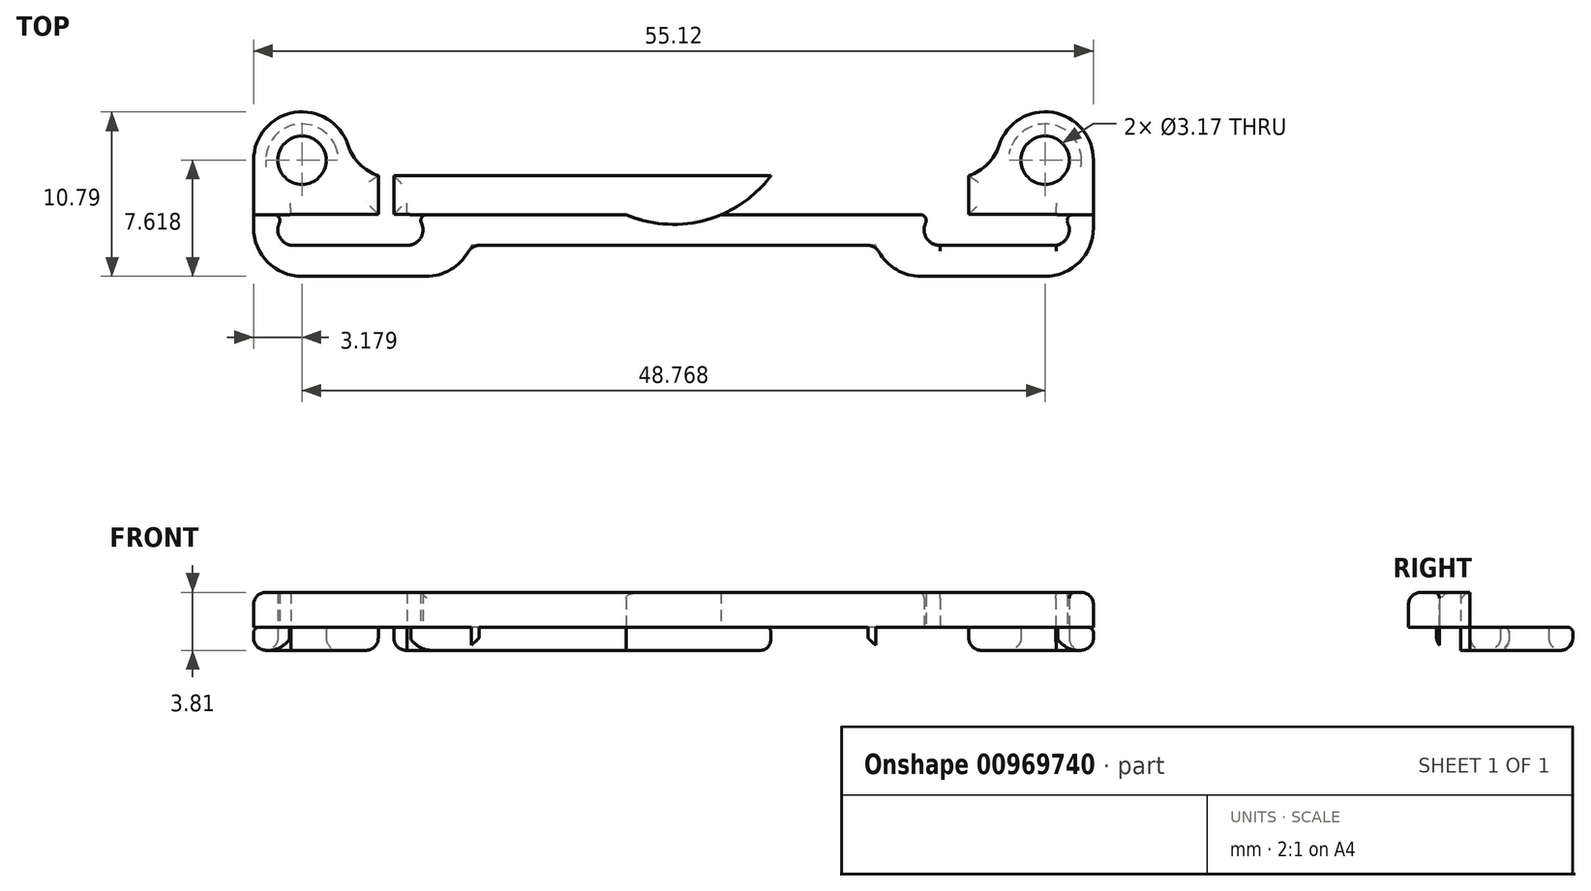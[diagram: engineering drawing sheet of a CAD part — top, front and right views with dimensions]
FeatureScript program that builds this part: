
annotation { "Feature Type Name" : "Feature", "Feature Type Description" : "" }
export const myFeature = defineFeature(function(context is Context, id is Id, definition is map)
    precondition{}
    {
        {
            var Q0;
            Q0=qCreatedBy(makeId("Top.planeOp"),FACE);
            var sketch = newSketch(context, id + "F0", { "sketchPlane" : qUnion([Q0])});
            skLineSegment(sketch, "E0", {"start": v(-29.34, -33.33) * mm, "end": v(-29.34, -17.07) * mm});
            skLineSegment(sketch, "E1", {"start": v(-32.75, -29.77) * mm, "end": v(29.96, -29.77) * mm, "construction": true});
            skLineSegment(sketch, "E2", {"start": v(-25.78, 34.73) * mm, "end": v(-25.78, -35.44) * mm, "construction": true});
            skLineSegment(sketch, "E3", {"start": v(22.99, 35.22) * mm, "end": v(22.99, -36.91) * mm, "construction": true});
            skCircle(sketch, "E4", {"center": v(-25.78, -29.77) * mm, "radius": 1.59 * mm});
            skCircle(sketch, "E5", {"center": v(22.99, -29.77) * mm, "radius": 1.59 * mm});
            skArc(sketch, "E6", {"start": v(-22.77, -30.79) * mm, "mid": v(-25.27, -26.64) * mm, "end": v(-28.96, -29.77) * mm});
            skArc(sketch, "E7", {"start": v(22.99, -32.95) * mm, "mid": v(24.84, -27.2) * mm, "end": v(19.98, -30.79) * mm});
            skLineSegment(sketch, "E8", {"start": v(-29.34, -33.33) * mm, "end": v(-29.34, -44.2) * mm});
            skLineSegment(sketch, "E9", {"start": v(-28.96, -37.4) * mm, "end": v(-14.67, -37.4) * mm});
            skLineSegment(sketch, "E10", {"start": v(-14.67, -35.36) * mm, "end": v(-14.67, -37.4) * mm});
            skLineSegment(sketch, "E11", {"start": v(-28.96, -29.77) * mm, "end": v(-28.96, -37.4) * mm});
            skLineSegment(sketch, "E12.trimOffspring", {"start": v(-18.84, -33.33) * mm, "end": v(-19.76, -33.33) * mm});
            skLineSegment(sketch, "E13.trimOffspring", {"start": v(-14.67, -35.36) * mm, "end": v(-1.4, -35.36) * mm});
            skPoint(sketch, "E14.orphan", {"position": v(-29.34, -37.4) * mm});
            skArc(sketch, "E15", {"start": v(-18.9, -35.36) * mm, "mid": v(-17.84, -34.35) * mm, "end": v(-18.88, -33.33) * mm});
            skArc(sketch, "E16", {"start": v(-26.5, -33.33) * mm, "mid": v(-27.37, -34.34) * mm, "end": v(-26.5, -35.36) * mm});
            skLineSegment(sketch, "E17", {"start": v(-19.76, -33.33) * mm, "end": v(-19.76, -30.79) * mm});
            skLineSegment(sketch, "E18", {"start": v(-20.77, -33.33) * mm, "end": v(-20.77, -30.79) * mm});
            skLineSegment(sketch, "E19.trimOffspring", {"start": v(-26.5, -35.36) * mm, "end": v(-18.82, -35.36) * mm});
            skLineSegment(sketch, "E20.trimOffspring", {"start": v(-27.37, -34.31) * mm, "end": v(-27.37, -34.37) * mm});
            skLineSegment(sketch, "E21.trimOffspring", {"start": v(-20.77, -33.33) * mm, "end": v(-26.5, -33.33) * mm});
            skLineSegment(sketch, "E22.trimOffspring", {"start": v(-19.76, -30.79) * mm, "end": v(-1.4, -30.79) * mm});
            skLineSegment(sketch, "E23.trimOffspring", {"start": v(-22.77, -30.79) * mm, "end": v(-20.77, -30.79) * mm});
            skLineSegment(sketch, "E24", {"start": v(-1.4, -30.79) * mm, "end": v(-1.4, -40.59) * mm});
            skLineSegment(sketch, "E25.MirrorCS", {"start": v(19.98, -30.79) * mm, "end": v(17.98, -30.79) * mm});
            skLineSegment(sketch, "E26.MirrorCS", {"start": v(17.98, -33.33) * mm, "end": v(17.98, -30.79) * mm});
            skLineSegment(sketch, "E27.MirrorCS", {"start": v(16.96, -33.33) * mm, "end": v(16.96, -30.79) * mm});
            skLineSegment(sketch, "E28.MirrorCS", {"start": v(16.96, -30.79) * mm, "end": v(-1.4, -30.79) * mm});
            skLineSegment(sketch, "E29.MirrorCS", {"start": v(16.04, -33.33) * mm, "end": v(16.96, -33.33) * mm});
            skArc(sketch, "E30.MirrorCS", {"start": v(16.1, -35.36) * mm, "mid": v(15.05, -34.35) * mm, "end": v(16.09, -33.33) * mm});
            skLineSegment(sketch, "E31.MirrorCS", {"start": v(23.7, -35.36) * mm, "end": v(16.03, -35.36) * mm});
            skArc(sketch, "E32.MirrorCS", {"start": v(23.7, -33.33) * mm, "mid": v(24.57, -34.34) * mm, "end": v(23.7, -35.36) * mm});
            skLineSegment(sketch, "E33.MirrorCS", {"start": v(17.98, -33.33) * mm, "end": v(23.7, -33.33) * mm});
            skLineSegment(sketch, "E34.MirrorCS", {"start": v(26.16, -29.77) * mm, "end": v(26.16, -37.4) * mm});
            skLineSegment(sketch, "E35.MirrorCS", {"start": v(26.16, -37.4) * mm, "end": v(11.87, -37.4) * mm});
            skLineSegment(sketch, "E36.MirrorCS", {"start": v(11.87, -35.36) * mm, "end": v(11.87, -37.4) * mm});
            skLineSegment(sketch, "E37.MirrorCS", {"start": v(11.87, -35.36) * mm, "end": v(-1.4, -35.36) * mm});
            skSolve(sketch);
        }
        {
            var Q0;
            Q0=makeQuery(id+"F0.imprint","IMPRINT",FACE,{"disambiguationData":[TD([[makeQuery(id+"F0.imprint","IMPRINT",EDGE,{"derivedFrom":sQuery(id+"F0.wireOp",EDGE,"E5")}),-1.0]])]});
            var Q1;
            Q1=makeQuery(id+"F0.imprint","IMPRINT",FACE,{"disambiguationData":[TD([[makeQuery(id+"F0.imprint","IMPRINT",EDGE,{"derivedFrom":sQuery(id+"F0.wireOp",EDGE,"E4")}),-1.0]])]});
            extrude(context, id + "F1", {"entities" : qUnion([Q0, Q1]), "depth" : 1.52 * mm, "offsetDistance" : 25.4 * mm});
        }
        {
            var Q0;
            Q0=makeQuery(id+"F1.opExtrude","CAP_FACE",FACE,{"disambiguationData":[OSD([sQuery(id+"F0.wireOp",EDGE,"E4"),sQuery(id+"F0.wireOp",EDGE,"E5"),sQuery(id+"F0.wireOp",EDGE,"E6"),sQuery(id+"F0.wireOp",EDGE,"E7"),sQuery(id+"F0.wireOp",EDGE,"E9"),sQuery(id+"F0.wireOp",EDGE,"E10"),sQuery(id+"F0.wireOp",EDGE,"E11"),sQuery(id+"F0.wireOp",EDGE,"E12.trimOffspring"),sQuery(id+"F0.wireOp",EDGE,"E13.trimOffspring"),sQuery(id+"F0.wireOp",EDGE,"E15"),sQuery(id+"F0.wireOp",EDGE,"E16"),sQuery(id+"F0.wireOp",EDGE,"E17"),sQuery(id+"F0.wireOp",EDGE,"E18"),sQuery(id+"F0.wireOp",EDGE,"E19.trimOffspring"),sQuery(id+"F0.wireOp",EDGE,"E21.trimOffspring"),sQuery(id+"F0.wireOp",EDGE,"E22.trimOffspring"),sQuery(id+"F0.wireOp",EDGE,"E23.trimOffspring"),sQuery(id+"F0.wireOp",EDGE,"E25.MirrorCS"),sQuery(id+"F0.wireOp",EDGE,"E26.MirrorCS"),sQuery(id+"F0.wireOp",EDGE,"E27.MirrorCS"),sQuery(id+"F0.wireOp",EDGE,"E28.MirrorCS"),sQuery(id+"F0.wireOp",EDGE,"E29.MirrorCS"),sQuery(id+"F0.wireOp",EDGE,"E30.MirrorCS"),sQuery(id+"F0.wireOp",EDGE,"E31.MirrorCS"),sQuery(id+"F0.wireOp",EDGE,"E32.MirrorCS"),sQuery(id+"F0.wireOp",EDGE,"E33.MirrorCS"),sQuery(id+"F0.wireOp",EDGE,"E34.MirrorCS"),sQuery(id+"F0.wireOp",EDGE,"E35.MirrorCS"),sQuery(id+"F0.wireOp",EDGE,"E36.MirrorCS"),sQuery(id+"F0.wireOp",EDGE,"E37.MirrorCS")])],"isStart":false});
            var sketch = newSketch(context, id + "F2", { "sketchPlane" : qUnion([Q0])});
            skLineSegment(sketch, "E38.bottom", {"start": v(-28.96, -37.4) * mm, "end": v(26.16, -37.4) * mm});
            skLineSegment(sketch, "E38.top", {"start": v(-28.96, -33.35) * mm, "end": v(26.16, -33.35) * mm});
            skLineSegment(sketch, "E38.left", {"start": v(-28.96, -37.4) * mm, "end": v(-28.96, -33.35) * mm});
            skLineSegment(sketch, "E38.right", {"start": v(26.16, -37.4) * mm, "end": v(26.16, -33.35) * mm});
            skLineSegment(sketch, "E39", {"start": v(-25.78, -29.77) * mm, "end": v(22.99, -29.77) * mm, "construction": true});
            skLineSegment(sketch, "E40", {"start": v(-1.4, -25.98) * mm, "end": v(-1.4, -33.98) * mm, "construction": true});
            skPoint(sketch, "E41.orphan", {"position": v(-1.4, -29.77) * mm});
            skPoint(sketch, "E42.orphan", {"position": v(-1.4, -33.35) * mm});
            skCircle(sketch, "E43", {"center": v(-1.4, -25.98) * mm, "radius": 8 * mm});
            skSolve(sketch);
        }
        {
            var Q0;
            {var subQ2=sQuery(id+"F2.wireOp",EDGE,"E38.left");Q0=makeQuery(id+"F2.imprint","IMPRINT",FACE,{"disambiguationData":[TD([[makeQuery(id+"F2.imprint","IMPRINT",EDGE,{"derivedFrom":subQ2}),1.0]])]});}
            extrude(context, id + "F3", {"entities" : qUnion([Q0]), "operationType" : NewBodyOperationType.ADD, "depth" : 2.3 * mm, "offsetDistance" : 25.4 * mm});
        }
        {
            var Q0;
            Q0=makeQuery(id+"F1.opExtrude","SWEPT_EDGE",EDGE,{"disambiguationData":[OSD([sQuery(id+"F0.wireOp",EDGE,"E6"),sQuery(id+"F0.wireOp",EDGE,"E23.trimOffspring")])]});
            var Q1;
            Q1=makeQuery(id+"F1.opExtrude","SWEPT_EDGE",EDGE,{"disambiguationData":[OSD([sQuery(id+"F0.wireOp",EDGE,"E7"),sQuery(id+"F0.wireOp",EDGE,"E25.MirrorCS")])]});
            var Q2;
            Q2=makeQuery(id+"F3.boolean.opBoolean","MERGE",EDGE,{"derivedFrom":[makeQuery(id+"F1.opExtrude","SWEPT_EDGE",EDGE,{"disambiguationData":[OSD([sQuery(id+"F0.wireOp",EDGE,"E34.MirrorCS"),sQuery(id+"F0.wireOp",EDGE,"E35.MirrorCS")])]}),makeQuery(id+"F3.opExtrude","SWEPT_EDGE",EDGE,{"disambiguationData":[OSD([sQuery(id+"F2.wireOp",EDGE,"E38.bottom"),sQuery(id+"F2.wireOp",EDGE,"E38.right")])]})]});
            var Q3;
            {var subQ0=sQuery(id+"F0.wireOp",EDGE,"E36.MirrorCS");Q3=makeQuery(id+"F3.boolean.opBoolean","MERGE",EDGE,{"derivedFrom":[makeQuery(id+"F1.opExtrude","SWEPT_EDGE",EDGE,{"disambiguationData":[OSD([sQuery(id+"F0.wireOp",EDGE,"E35.MirrorCS"),subQ0])]}),makeQuery(id+"F3.opExtrude","SWEPT_EDGE",EDGE,{"disambiguationData":[OSD([subQ0,sQuery(id+"F2.wireOp",EDGE,"E38.bottom")])]})]});}
            var Q4;
            {var subQ0=sQuery(id+"F0.wireOp",EDGE,"E10");Q4=makeQuery(id+"F3.boolean.opBoolean","MERGE",EDGE,{"derivedFrom":[makeQuery(id+"F1.opExtrude","SWEPT_EDGE",EDGE,{"disambiguationData":[OSD([sQuery(id+"F0.wireOp",EDGE,"E9"),subQ0])]}),makeQuery(id+"F3.opExtrude","SWEPT_EDGE",EDGE,{"disambiguationData":[OSD([subQ0,sQuery(id+"F2.wireOp",EDGE,"E38.bottom")])]})]});}
            var Q5;
            Q5=makeQuery(id+"F3.boolean.opBoolean","MERGE",EDGE,{"derivedFrom":[makeQuery(id+"F1.opExtrude","SWEPT_EDGE",EDGE,{"disambiguationData":[OSD([sQuery(id+"F0.wireOp",EDGE,"E9"),sQuery(id+"F0.wireOp",EDGE,"E11")])]}),makeQuery(id+"F3.opExtrude","SWEPT_EDGE",EDGE,{"disambiguationData":[OSD([sQuery(id+"F2.wireOp",EDGE,"E38.bottom"),sQuery(id+"F2.wireOp",EDGE,"E38.left")])]})]});
            fillet(context, id + "F4", {"entities" : qUnion([Q0, Q1, Q2, Q3, Q4, Q5]), "radius" : 3.17 * mm, "tangentPropagation" : true, "allowEdgeOverflow" : false});
        }
        {
            var Q0;
            {var subQ0=sQuery(id+"F0.wireOp",EDGE,"E37.MirrorCS");var subQ1=sQuery(id+"F0.wireOp",EDGE,"E13.trimOffspring");var subQ2=sQuery(id+"F0.wireOp",EDGE,"E10");Q0=makeQuery(id+"F4.opFillet","BLEND_EDGE",EDGE,{"blendedFrom":[makeQuery(id+"F3.boolean.opBoolean","MERGE",EDGE,{"derivedFrom":[makeQuery(id+"F1.opExtrude","SWEPT_EDGE",EDGE,{"disambiguationData":[OSD([sQuery(id+"F0.wireOp",EDGE,"E9"),subQ2])]}),makeQuery(id+"F3.opExtrude","SWEPT_EDGE",EDGE,{"disambiguationData":[OSD([subQ2,sQuery(id+"F2.wireOp",EDGE,"E38.bottom")])]})]}),makeQuery(id+"F3.boolean.opBoolean","MERGE",FACE,{"derivedFrom":[makeQuery(id+"F1.opExtrude","SWEPT_FACE",FACE,{"disambiguationData":[OSD([subQ1,subQ0])]}),makeQuery(id+"F3.opExtrude","SWEPT_FACE",FACE,{"disambiguationData":[OSD([subQ1,subQ0])]})]})],"blendedInto":[makeQuery(id+"F3.boolean.opBoolean","MERGE",FACE,{"derivedFrom":[makeQuery(id+"F1.opExtrude","SWEPT_FACE",FACE,{"disambiguationData":[OSD([subQ1,subQ0])]}),makeQuery(id+"F3.opExtrude","SWEPT_FACE",FACE,{"disambiguationData":[OSD([subQ1,subQ0])]})]})]});}
            var Q1;
            {var subQ0=sQuery(id+"F0.wireOp",EDGE,"E37.MirrorCS");var subQ1=sQuery(id+"F0.wireOp",EDGE,"E13.trimOffspring");var subQ2=sQuery(id+"F0.wireOp",EDGE,"E36.MirrorCS");Q1=makeQuery(id+"F4.opFillet","BLEND_EDGE",EDGE,{"blendedFrom":[makeQuery(id+"F3.boolean.opBoolean","MERGE",EDGE,{"derivedFrom":[makeQuery(id+"F1.opExtrude","SWEPT_EDGE",EDGE,{"disambiguationData":[OSD([sQuery(id+"F0.wireOp",EDGE,"E35.MirrorCS"),subQ2])]}),makeQuery(id+"F3.opExtrude","SWEPT_EDGE",EDGE,{"disambiguationData":[OSD([subQ2,sQuery(id+"F2.wireOp",EDGE,"E38.bottom")])]})]}),makeQuery(id+"F3.boolean.opBoolean","MERGE",FACE,{"derivedFrom":[makeQuery(id+"F1.opExtrude","SWEPT_FACE",FACE,{"disambiguationData":[OSD([subQ1,subQ0])]}),makeQuery(id+"F3.opExtrude","SWEPT_FACE",FACE,{"disambiguationData":[OSD([subQ1,subQ0])]})]})],"blendedInto":[makeQuery(id+"F3.boolean.opBoolean","MERGE",FACE,{"derivedFrom":[makeQuery(id+"F1.opExtrude","SWEPT_FACE",FACE,{"disambiguationData":[OSD([subQ1,subQ0])]}),makeQuery(id+"F3.opExtrude","SWEPT_FACE",FACE,{"disambiguationData":[OSD([subQ1,subQ0])]})]})]});}
            var Q2;
            Q2=makeQuery(id+"F1.opExtrude","CAP_FACE",FACE,{"disambiguationData":[OSD([sQuery(id+"F0.wireOp",EDGE,"E4"),sQuery(id+"F0.wireOp",EDGE,"E5"),sQuery(id+"F0.wireOp",EDGE,"E6"),sQuery(id+"F0.wireOp",EDGE,"E7"),sQuery(id+"F0.wireOp",EDGE,"E9"),sQuery(id+"F0.wireOp",EDGE,"E10"),sQuery(id+"F0.wireOp",EDGE,"E11"),sQuery(id+"F0.wireOp",EDGE,"E12.trimOffspring"),sQuery(id+"F0.wireOp",EDGE,"E13.trimOffspring"),sQuery(id+"F0.wireOp",EDGE,"E15"),sQuery(id+"F0.wireOp",EDGE,"E16"),sQuery(id+"F0.wireOp",EDGE,"E17"),sQuery(id+"F0.wireOp",EDGE,"E18"),sQuery(id+"F0.wireOp",EDGE,"E19.trimOffspring"),sQuery(id+"F0.wireOp",EDGE,"E21.trimOffspring"),sQuery(id+"F0.wireOp",EDGE,"E22.trimOffspring"),sQuery(id+"F0.wireOp",EDGE,"E23.trimOffspring"),sQuery(id+"F0.wireOp",EDGE,"E25.MirrorCS"),sQuery(id+"F0.wireOp",EDGE,"E26.MirrorCS"),sQuery(id+"F0.wireOp",EDGE,"E27.MirrorCS"),sQuery(id+"F0.wireOp",EDGE,"E28.MirrorCS"),sQuery(id+"F0.wireOp",EDGE,"E29.MirrorCS"),sQuery(id+"F0.wireOp",EDGE,"E30.MirrorCS"),sQuery(id+"F0.wireOp",EDGE,"E31.MirrorCS"),sQuery(id+"F0.wireOp",EDGE,"E32.MirrorCS"),sQuery(id+"F0.wireOp",EDGE,"E33.MirrorCS"),sQuery(id+"F0.wireOp",EDGE,"E34.MirrorCS"),sQuery(id+"F0.wireOp",EDGE,"E35.MirrorCS"),sQuery(id+"F0.wireOp",EDGE,"E36.MirrorCS"),sQuery(id+"F0.wireOp",EDGE,"E37.MirrorCS")])],"isStart":true});
            fillet(context, id + "F5", {"entities" : qUnion([Q0, Q1, Q2]), "radius" : 0.81 * mm, "tangentPropagation" : true, "allowEdgeOverflow" : false});
        }
        {
            var Q0;
            Q0=makeQuery(id+"F3.opExtrude","CAP_EDGE",EDGE,{"disambiguationData":[OSD([sQuery(id+"F2.wireOp",EDGE,"E38.right")])],"isStart":false});
            fillet(context, id + "F6", {"entities" : qUnion([Q0]), "radius" : 0.81 * mm, "tangentPropagation" : true, "allowEdgeOverflow" : false});
        }
        {
            var Q0;
            Q0=makeQuery(id+"F1.opExtrude","CAP_EDGE",EDGE,{"disambiguationData":[OSD([sQuery(id+"F0.wireOp",EDGE,"E34.MirrorCS")])],"isStart":false});
            var Q1;
            Q1=makeQuery(id+"F1.opExtrude","CAP_EDGE",EDGE,{"disambiguationData":[OSD([sQuery(id+"F0.wireOp",EDGE,"E22.trimOffspring"),sQuery(id+"F0.wireOp",EDGE,"E28.MirrorCS")])],"isStart":false});
            var Q2;
            {var subQ0=sQuery(id+"F0.wireOp",EDGE,"E16");var subQ1=sQuery(id+"F0.wireOp",EDGE,"E11");var subQ3=sQuery(id+"F0.wireOp",EDGE,"E6");var subQ4=sQuery(id+"F0.wireOp",EDGE,"E4");var subQ5=sQuery(id+"F0.wireOp",EDGE,"E18");var subQ6=sQuery(id+"F0.wireOp",EDGE,"E21.trimOffspring");var subQ8=sQuery(id+"F0.wireOp",EDGE,"E23.trimOffspring");Q2=makeQuery(id+"F4.opFillet","BLEND_EDGE",EDGE,{"blendedFrom":[makeQuery(id+"F1.opExtrude","SWEPT_EDGE",EDGE,{"disambiguationData":[OSD([subQ3,subQ8])]}),makeQuery(id+"F3.boolean.opBoolean","SPLIT",FACE,{"disambiguationData":[TD([makeQuery(id+"F1.opExtrude","SWEPT_FACE",FACE,{"disambiguationData":[OSD([subQ4])]})])],"derivedFrom":makeQuery(id+"F1.opExtrude","CAP_FACE",FACE,{"disambiguationData":[OSD([subQ4,sQuery(id+"F0.wireOp",EDGE,"E5"),subQ3,sQuery(id+"F0.wireOp",EDGE,"E7"),sQuery(id+"F0.wireOp",EDGE,"E9"),sQuery(id+"F0.wireOp",EDGE,"E10"),subQ1,sQuery(id+"F0.wireOp",EDGE,"E12.trimOffspring"),sQuery(id+"F0.wireOp",EDGE,"E13.trimOffspring"),sQuery(id+"F0.wireOp",EDGE,"E15"),subQ0,sQuery(id+"F0.wireOp",EDGE,"E17"),subQ5,sQuery(id+"F0.wireOp",EDGE,"E19.trimOffspring"),subQ6,sQuery(id+"F0.wireOp",EDGE,"E22.trimOffspring"),subQ8,sQuery(id+"F0.wireOp",EDGE,"E25.MirrorCS"),sQuery(id+"F0.wireOp",EDGE,"E26.MirrorCS"),sQuery(id+"F0.wireOp",EDGE,"E27.MirrorCS"),sQuery(id+"F0.wireOp",EDGE,"E28.MirrorCS"),sQuery(id+"F0.wireOp",EDGE,"E29.MirrorCS"),sQuery(id+"F0.wireOp",EDGE,"E30.MirrorCS"),sQuery(id+"F0.wireOp",EDGE,"E31.MirrorCS"),sQuery(id+"F0.wireOp",EDGE,"E32.MirrorCS"),sQuery(id+"F0.wireOp",EDGE,"E33.MirrorCS"),sQuery(id+"F0.wireOp",EDGE,"E34.MirrorCS"),sQuery(id+"F0.wireOp",EDGE,"E35.MirrorCS"),sQuery(id+"F0.wireOp",EDGE,"E36.MirrorCS"),sQuery(id+"F0.wireOp",EDGE,"E37.MirrorCS")])],"isStart":false})})],"blendedInto":[makeQuery(id+"F3.boolean.opBoolean","SPLIT",FACE,{"disambiguationData":[TD([makeQuery(id+"F1.opExtrude","SWEPT_FACE",FACE,{"disambiguationData":[OSD([subQ4])]})])],"derivedFrom":makeQuery(id+"F1.opExtrude","CAP_FACE",FACE,{"disambiguationData":[OSD([subQ4,sQuery(id+"F0.wireOp",EDGE,"E5"),subQ3,sQuery(id+"F0.wireOp",EDGE,"E7"),sQuery(id+"F0.wireOp",EDGE,"E9"),sQuery(id+"F0.wireOp",EDGE,"E10"),subQ1,sQuery(id+"F0.wireOp",EDGE,"E12.trimOffspring"),sQuery(id+"F0.wireOp",EDGE,"E13.trimOffspring"),sQuery(id+"F0.wireOp",EDGE,"E15"),subQ0,sQuery(id+"F0.wireOp",EDGE,"E17"),subQ5,sQuery(id+"F0.wireOp",EDGE,"E19.trimOffspring"),subQ6,sQuery(id+"F0.wireOp",EDGE,"E22.trimOffspring"),subQ8,sQuery(id+"F0.wireOp",EDGE,"E25.MirrorCS"),sQuery(id+"F0.wireOp",EDGE,"E26.MirrorCS"),sQuery(id+"F0.wireOp",EDGE,"E27.MirrorCS"),sQuery(id+"F0.wireOp",EDGE,"E28.MirrorCS"),sQuery(id+"F0.wireOp",EDGE,"E29.MirrorCS"),sQuery(id+"F0.wireOp",EDGE,"E30.MirrorCS"),sQuery(id+"F0.wireOp",EDGE,"E31.MirrorCS"),sQuery(id+"F0.wireOp",EDGE,"E32.MirrorCS"),sQuery(id+"F0.wireOp",EDGE,"E33.MirrorCS"),sQuery(id+"F0.wireOp",EDGE,"E34.MirrorCS"),sQuery(id+"F0.wireOp",EDGE,"E35.MirrorCS"),sQuery(id+"F0.wireOp",EDGE,"E36.MirrorCS"),sQuery(id+"F0.wireOp",EDGE,"E37.MirrorCS")])],"isStart":false})})]});}
            var Q3;
            Q3=makeQuery(id+"F3.opExtrude","SWEPT_EDGE",EDGE,{"disambiguationData":[OSD([sQuery(id+"F0.wireOp",EDGE,"E32.MirrorCS"),sQuery(id+"F2.wireOp",EDGE,"E38.top")])]});
            var Q4;
            Q4=makeQuery(id+"F3.opExtrude","SWEPT_EDGE",EDGE,{"disambiguationData":[OSD([sQuery(id+"F0.wireOp",EDGE,"E16"),sQuery(id+"F2.wireOp",EDGE,"E38.top")])]});
            var Q5;
            Q5=makeQuery(id+"F3.opExtrude","SWEPT_EDGE",EDGE,{"disambiguationData":[OSD([sQuery(id+"F0.wireOp",EDGE,"E30.MirrorCS"),sQuery(id+"F2.wireOp",EDGE,"E38.top")])]});
            var Q6;
            Q6=makeQuery(id+"F3.opExtrude","SWEPT_EDGE",EDGE,{"disambiguationData":[OSD([sQuery(id+"F0.wireOp",EDGE,"E15"),sQuery(id+"F2.wireOp",EDGE,"E38.top")])]});
            var Q7;
            {var subQ0=sQuery(id+"F2.wireOp",EDGE,"E38.top");Q7=makeQuery(id+"F3.opExtrude","CAP_EDGE",EDGE,{"disambiguationData":[OSD([subQ0]),TDD([makeQuery(id+"F2.imprint","IMPRINT",EDGE,{"disambiguationData":[TD([[makeQuery(id+"F2.imprint","INTERSECT",VERTEX,{"derivedFrom":[makeQuery(id+"F1.opExtrude","CAP_EDGE",EDGE,{"disambiguationData":[OSD([sQuery(id+"F0.wireOp",EDGE,"E15")])],"isStart":false}),subQ0]}),-1.0]])],"derivedFrom":subQ0})])],"isStart":false});}
            var Q8;
            {var subQ0=sQuery(id+"F2.wireOp",EDGE,"E38.top");Q8=makeQuery(id+"F3.opExtrude","CAP_EDGE",EDGE,{"disambiguationData":[OSD([subQ0]),TDD([makeQuery(id+"F2.imprint","IMPRINT",EDGE,{"disambiguationData":[TD([[makeQuery(id+"F2.imprint","INTERSECT",VERTEX,{"derivedFrom":[makeQuery(id+"F1.opExtrude","CAP_EDGE",EDGE,{"disambiguationData":[OSD([sQuery(id+"F0.wireOp",EDGE,"E15")])],"isStart":false}),subQ0]}),-1.0]])],"derivedFrom":subQ0})])],"isStart":true});}
            var Q9;
            {var subQ0=sQuery(id+"F2.wireOp",EDGE,"E38.top");Q9=makeQuery(id+"F3.opExtrude","CAP_EDGE",EDGE,{"disambiguationData":[OSD([subQ0]),TDD([makeQuery(id+"F2.imprint","IMPRINT",EDGE,{"disambiguationData":[TD([[makeQuery(id+"F2.imprint","INTERSECT",VERTEX,{"disambiguationData":[OD(1.0)],"derivedFrom":[subQ0,sQuery(id+"F2.wireOp",EDGE,"E43")]}),-1.0]])],"derivedFrom":subQ0})])],"isStart":true});}
            var Q10;
            {var subQ0=sQuery(id+"F2.wireOp",EDGE,"E38.top");Q10=makeQuery(id+"F3.opExtrude","CAP_EDGE",EDGE,{"disambiguationData":[OSD([subQ0]),TDD([makeQuery(id+"F2.imprint","IMPRINT",EDGE,{"disambiguationData":[TD([[makeQuery(id+"F2.imprint","INTERSECT",VERTEX,{"disambiguationData":[OD(1.0)],"derivedFrom":[subQ0,sQuery(id+"F2.wireOp",EDGE,"E43")]}),-1.0]])],"derivedFrom":subQ0})])],"isStart":false});}
            var Q11;
            Q11=makeQuery(id+"F3.opExtrude","CAP_EDGE",EDGE,{"disambiguationData":[OSD([sQuery(id+"F0.wireOp",EDGE,"E30.MirrorCS")])],"isStart":false});
            var Q12;
            Q12=makeQuery(id+"F3.opExtrude","CAP_EDGE",EDGE,{"disambiguationData":[OSD([sQuery(id+"F0.wireOp",EDGE,"E31.MirrorCS")])],"isStart":false});
            var Q13;
            Q13=makeQuery(id+"F3.opExtrude","CAP_EDGE",EDGE,{"disambiguationData":[OSD([sQuery(id+"F0.wireOp",EDGE,"E32.MirrorCS")])],"isStart":false});
            fillet(context, id + "F7", {"entities" : qUnion([Q0, Q1, Q2, Q3, Q4, Q5, Q6, Q7, Q8, Q9, Q10, Q11, Q12, Q13]), "radius" : 0.38 * mm, "tangentPropagation" : true, "allowEdgeOverflow" : false});
        }
        {
            var Q0;
            {var subQ0=sQuery(id+"F2.wireOp",EDGE,"E43");var subQ1=makeQuery(id+"F1.opExtrude","CAP_EDGE",EDGE,{"disambiguationData":[OSD([sQuery(id+"F0.wireOp",EDGE,"E22.trimOffspring"),sQuery(id+"F0.wireOp",EDGE,"E28.MirrorCS")])],"isStart":false});var subQ2=makeQuery(id+"F2.imprint","INTERSECT",VERTEX,{"disambiguationData":[OD(0.0)],"derivedFrom":[subQ1,subQ0]});Q0=makeQuery(id+"F2.imprint","IMPRINT",FACE,{"disambiguationData":[TD([[makeQuery(id+"F2.imprint","IMPRINT",EDGE,{"disambiguationData":[TD([[subQ2,1.0]])],"derivedFrom":subQ0}),1.0]])]});}
            var Q1;
            {var subQ0=sQuery(id+"F2.wireOp",EDGE,"E43");var subQ1=sQuery(id+"F2.wireOp",EDGE,"E38.top");var subQ2=makeQuery(id+"F2.imprint","INTERSECT",VERTEX,{"disambiguationData":[OD(0.0)],"derivedFrom":[subQ1,subQ0]});Q1=makeQuery(id+"F2.imprint","IMPRINT",FACE,{"disambiguationData":[TD([[makeQuery(id+"F2.imprint","IMPRINT",EDGE,{"disambiguationData":[TD([[subQ2,-1.0]])],"derivedFrom":subQ1}),-1.0]])]});}
            var Q2;
            {var subQ0=sQuery(id+"F2.wireOp",EDGE,"E43");var subQ1=sQuery(id+"F2.wireOp",EDGE,"E38.top");var subQ2=makeQuery(id+"F2.imprint","INTERSECT",VERTEX,{"disambiguationData":[OD(0.0)],"derivedFrom":[subQ1,subQ0]});Q2=makeQuery(id+"F2.imprint","IMPRINT",FACE,{"disambiguationData":[TD([[makeQuery(id+"F2.imprint","IMPRINT",EDGE,{"disambiguationData":[TD([[subQ2,-1.0]])],"derivedFrom":subQ1}),1.0]])]});}
            extrude(context, id + "F8", {"entities" : qUnion([Q0, Q1, Q2]), "operationType" : NewBodyOperationType.REMOVE, "oppositeDirection" : true, "depth" : 5.08 * mm, "offsetDistance" : 25.4 * mm});
        }
    });
